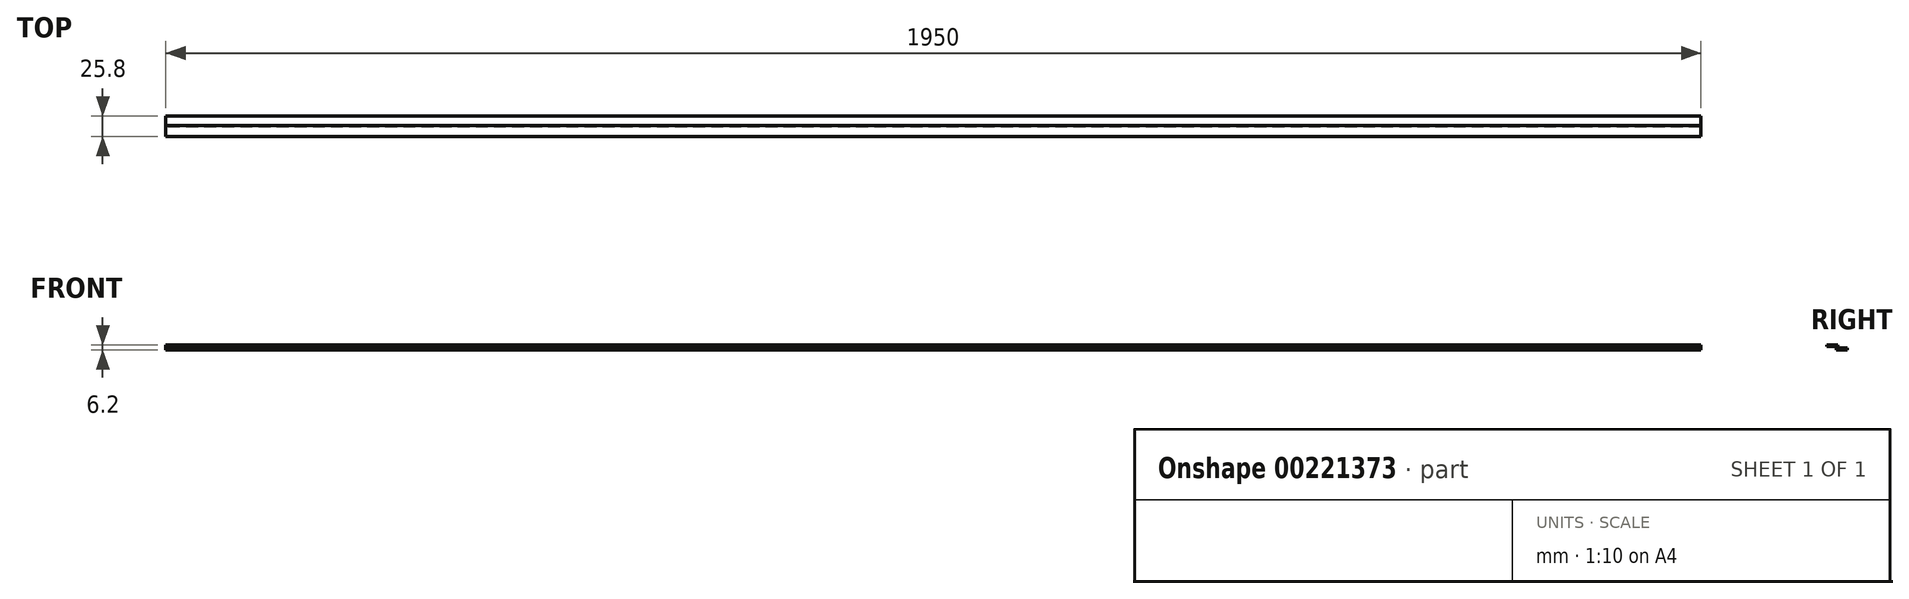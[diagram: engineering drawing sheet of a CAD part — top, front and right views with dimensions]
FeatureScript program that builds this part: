
annotation { "Feature Type Name" : "Feature", "Feature Type Description" : "" }
export const myFeature = defineFeature(function(context is Context, id is Id, definition is map)
    precondition{}
    {
        {
            var Q0;
            Q0=qCreatedBy(makeId("Right.planeOp"),FACE);
            var sketch = newSketch(context, id + "F0", { "sketchPlane" : qUnion([Q0])});
            skLineSegment(sketch, "E0", {"start": v(0, 0) * mm, "end": v(0, -4) * mm});
            skLineSegment(sketch, "E1", {"start": v(0, -4) * mm, "end": v(11.8, -4) * mm});
            skLineSegment(sketch, "E2", {"start": v(11.8, -4) * mm, "end": v(11.8, -6.2) * mm});
            skLineSegment(sketch, "E3", {"start": v(11.8, -6.2) * mm, "end": v(-2.2, -6.2) * mm});
            skLineSegment(sketch, "E4", {"start": v(-2.2, -6.2) * mm, "end": v(-2.2, -2.2) * mm});
            skLineSegment(sketch, "E5", {"start": v(-2.2, -2.2) * mm, "end": v(-14, -2.2) * mm});
            skLineSegment(sketch, "E6", {"start": v(-14, -2.2) * mm, "end": v(-14, 0) * mm});
            skLineSegment(sketch, "E7", {"start": v(-14, 0) * mm, "end": v(0, 0) * mm});
            skSolve(sketch);
        }
        {
            var Q0;
            Q0 = qSketchRegion(id + "F0", true);
            extrude(context, id + "F1", {"entities" : qUnion([Q0]), "depth" : 1950 * mm, "symmetric" : true});
        }
    });
